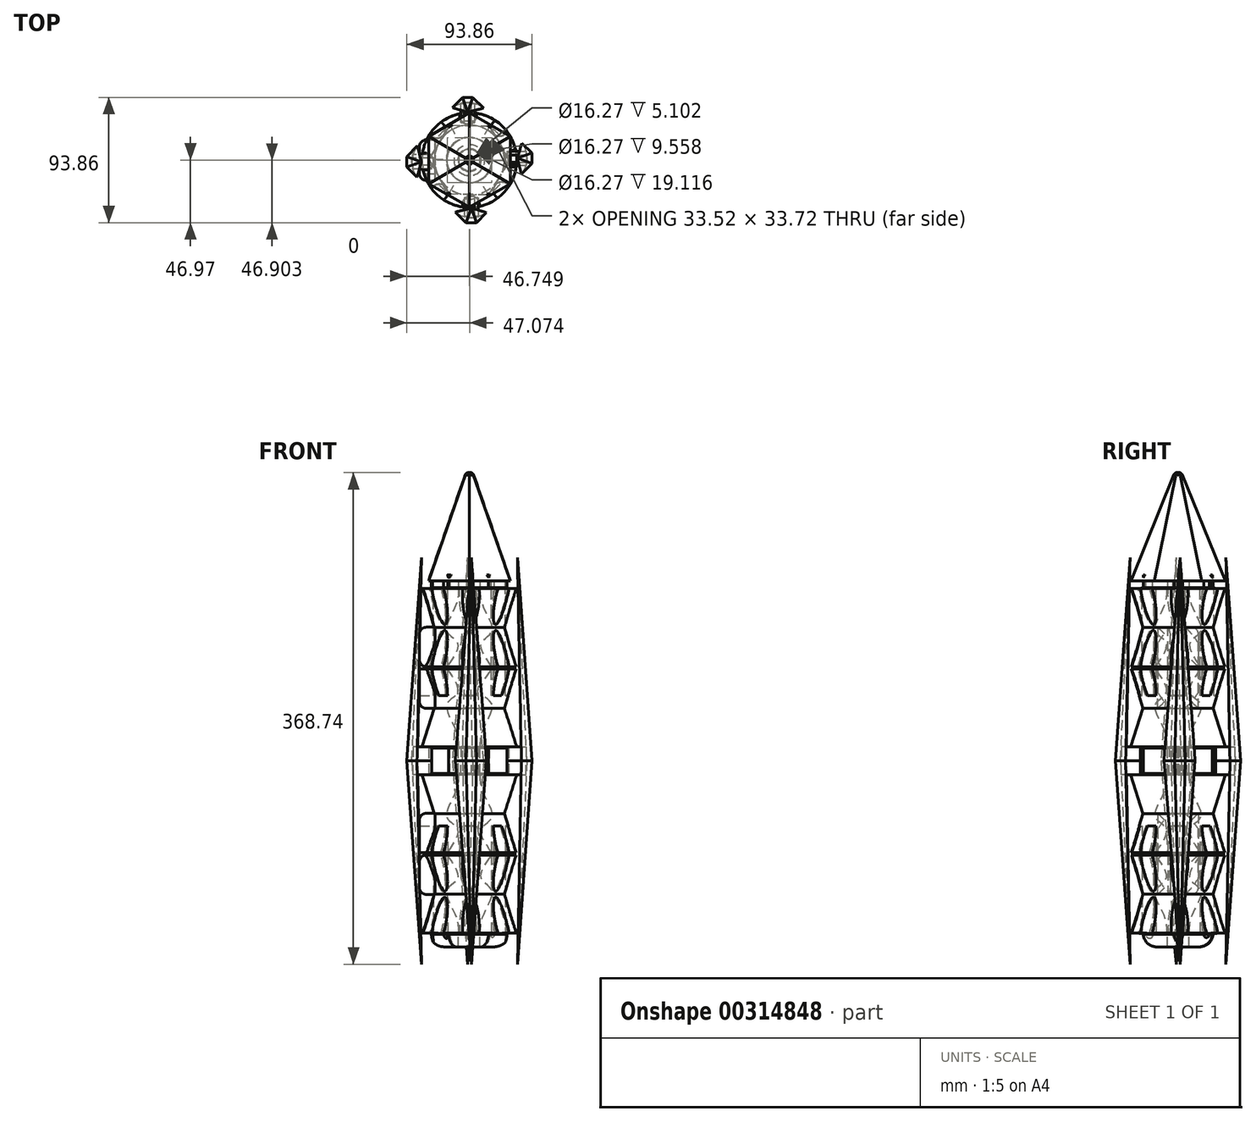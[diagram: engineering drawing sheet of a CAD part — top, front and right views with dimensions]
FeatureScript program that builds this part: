
annotation { "Feature Type Name" : "Feature", "Feature Type Description" : "" }
export const myFeature = defineFeature(function(context is Context, id is Id, definition is map)
    precondition{}
    {
        {
            var Q0;
            Q0=qCreatedBy(makeId("Front.planeOp"),FACE);
            var sketch = newSketch(context, id + "F0", { "sketchPlane" : qUnion([Q0])});
            skLineSegment(sketch, "E0", {"start": v(-35.52, -26.7) * mm, "end": v(-16.9, -26.7) * mm});
            skLineSegment(sketch, "E1", {"start": v(-16.9, 32.53) * mm, "end": v(-35.52, 31.8) * mm});
            skLineSegment(sketch, "E2", {"start": v(-35.52, 31.8) * mm, "end": v(-26.27, 2.74) * mm});
            skLineSegment(sketch, "E3", {"start": v(-26.27, 2.74) * mm, "end": v(-35.52, -26.7) * mm});
            skLineSegment(sketch, "E4", {"start": v(-8.14, 32.78) * mm, "end": v(-16.9, 32.53) * mm});
            skLineSegment(sketch, "E5", {"start": v(0, 39) * mm, "end": v(0, -30.84) * mm});
            skPoint(sketch, "E6.2.internal.orphan", {"position": v(-7.55, 0) * mm});
            skFitSpline(sketch, "E7", {"points": [v(-16.9, -26.7) * mm, v(-8.95, -8.9) * mm, v(-16.9, 0) * mm, v(-10.54, 18.32) * mm, v(-8.14, 32.78) * mm], "startDerivative": vector(53.05, 73.72) * mm, "endDerivative": vector(1.19, 56.97) * mm});
            skSolve(sketch);
        }
        {
            var Q0;
            Q0=makeQuery(id+"F0.imprint","IMPRINT",FACE,{"disambiguationData":[TD([[makeQuery(id+"F0.imprint","IMPRINT",EDGE,{"derivedFrom":sQuery(id+"F0.wireOp",EDGE,"E0")}),1.0]])]});
            var Q1;
            Q1=sQuery(id+"F0.wireOp",EDGE,"E5");
            revolve(context, id + "F1", {"entities" : qUnion([Q0]), "axis" : qUnion([Q1]), "revolveType" : RevolveType.FULL});
        }
        {
            var Q0;
            Q0=qCreatedBy(makeId("Top.planeOp"),FACE);
            cPlane(context, id + "F2", {"entities" : qUnion([Q0]), "cplaneType" : CPlaneType.OFFSET, "offset" : 32.68 * mm, "width" : 152.4 * mm, "height" : 152.4 * mm});
        }
        {
            var Q0;
            Q0=qCreatedBy(id+"F2.planeOp",FACE);
            var sketch = newSketch(context, id + "F3", { "sketchPlane" : qUnion([Q0])});
            skCircle(sketch, "E8.cCircle", {"center": v(-0.18, 0.04) * mm, "radius": 29.91 * mm, "construction": true});
            skLineSegment(sketch, "E8.0", {"start": v(15.3, 25.63) * mm, "end": v(29.72, -0.57) * mm});
            skLineSegment(sketch, "E8.1", {"start": v(29.72, -0.57) * mm, "end": v(14.24, -26.16) * mm});
            skLineSegment(sketch, "E8.2", {"start": v(14.24, -26.16) * mm, "end": v(-15.66, -25.55) * mm});
            skLineSegment(sketch, "E8.3", {"start": v(-15.66, -25.55) * mm, "end": v(-30.09, 0.65) * mm});
            skLineSegment(sketch, "E8.4", {"start": v(-30.09, 0.65) * mm, "end": v(-14.6, 26.25) * mm});
            skLineSegment(sketch, "E8.5", {"start": v(-14.6, 26.25) * mm, "end": v(15.3, 25.63) * mm});
            skCircle(sketch, "E9", {"center": v(-0.18, 0.04) * mm, "radius": 8.14 * mm});
            skSolve(sketch);
        }
        {
            var Q0;
            Q0=makeQuery(id+"F3.imprint","IMPRINT",FACE,{"disambiguationData":[TD([[makeQuery(id+"F3.imprint","IMPRINT",EDGE,{"derivedFrom":sQuery(id+"F3.wireOp",EDGE,"E8.0")}),-1.0]])]});
            extrude(context, id + "F4", {"entities" : qUnion([Q0]), "operationType" : NewBodyOperationType.ADD, "depth" : 9.56 * mm});
        }
        {
            var Q0;
            Q0=qCreatedBy(makeId("Front.planeOp"),FACE);
            var sketch = newSketch(context, id + "F5", { "sketchPlane" : qUnion([Q0])});
            skLineSegment(sketch, "E10.bottom", {"start": v(-25.84, 2.9) * mm, "end": v(-37.47, 2.9) * mm});
            skLineSegment(sketch, "E10.top", {"start": v(-25.84, -26.7) * mm, "end": v(-37.47, -26.7) * mm});
            skLineSegment(sketch, "E10.left", {"start": v(-25.84, 2.9) * mm, "end": v(-25.84, -26.7) * mm});
            skLineSegment(sketch, "E10.right", {"start": v(-37.47, 2.9) * mm, "end": v(-37.47, -26.7) * mm});
            skSolve(sketch);
        }
        {
            var Q0;
            Q0=makeQuery(id+"F5.imprint","IMPRINT",FACE,{"disambiguationData":[TD([[makeQuery(id+"F5.imprint","IMPRINT",EDGE,{"derivedFrom":sQuery(id+"F5.wireOp",EDGE,"E10.bottom")}),1.0]])]});
            extrude(context, id + "F6", {"entities" : qUnion([Q0]), "operationType" : NewBodyOperationType.ADD, "endBound" : BoundingType.SYMMETRIC, "depth" : 30.43 * mm});
        }
        {
            var Q0;
            Q0=makeQuery(id+"F1.opRevolve","SWEPT_FACE",FACE,{"disambiguationData":[OSD([sQuery(id+"F0.wireOp",EDGE,"E0")])]});
            cPlane(context, id + "F7", {"entities" : qUnion([Q0]), "cplaneType" : CPlaneType.OFFSET, "offset" : 0.85 * mm, "width" : 152.4 * mm, "height" : 152.4 * mm});
        }
        {
            var Q0;
            Q0=makeQuery(id+"F1.opRevolve","SWEPT_BODY",BODY,{"disambiguationData":[OSD([sQuery(id+"F0.wireOp",EDGE,"E0"),sQuery(id+"F0.wireOp",EDGE,"E1"),sQuery(id+"F0.wireOp",EDGE,"E2"),sQuery(id+"F0.wireOp",EDGE,"E3"),sQuery(id+"F0.wireOp",EDGE,"E4"),sQuery(id+"F0.wireOp",EDGE,"E7")])]});
            var Q1;
            Q1=qCreatedBy(id+"F7.planeOp",FACE);
            mirror(context, id + "F8", {"entities" : qUnion([Q0]), "mirrorPlane" : qUnion([Q1])});
        }
        {
            var Q0;
            Q0=qCreatedBy(makeId("Top.planeOp"),FACE);
            var sketch = newSketch(context, id + "F9", { "sketchPlane" : qUnion([Q0])});
            skCircle(sketch, "E11", {"center": v(-33.27, -1.11) * mm, "radius": 6.35 * mm});
            skSolve(sketch);
        }
        {
            var Q0;
            Q0 = qSketchRegion(id + "F9", true);
            extrude(context, id + "F10", {"entities" : qUnion([Q0]), "endBound" : BoundingType.SYMMETRIC, "oppositeDirection" : true, "depth" : 97.03 * mm});
        }
        {
            var Q0;
            Q0=makeQuery(id+"F10.opExtrude","CAP_EDGE",EDGE,{"disambiguationData":[OSD([sQuery(id+"F9.wireOp",EDGE,"E11")])],"isStart":true});
            fillet(context, id + "F11", {"entities" : qUnion([Q0]), "radius" : 5.08 * mm, "tangentPropagation" : true, "allowEdgeOverflow" : false});
        }
        {
            var Q0;
            Q0=makeQuery(id+"F6.opExtrude","SWEPT_EDGE",EDGE,{"disambiguationData":[OSD([sQuery(id+"F5.wireOp",EDGE,"E10.bottom"),sQuery(id+"F5.wireOp",EDGE,"E10.right")])]});
            var Q1;
            Q1=makeQuery(id+"F8.opPattern","COPY",EDGE,{"derivedFrom":makeQuery(id+"F6.opExtrude","SWEPT_EDGE",EDGE,{"disambiguationData":[OSD([sQuery(id+"F5.wireOp",EDGE,"E10.bottom"),sQuery(id+"F5.wireOp",EDGE,"E10.right")])]}),"instanceName":"1"});
            var Q2;
            Q2=makeQuery(id+"F8.opPattern","COPY",EDGE,{"derivedFrom":makeQuery(id+"F6.opExtrude","CAP_EDGE",EDGE,{"disambiguationData":[OSD([sQuery(id+"F5.wireOp",EDGE,"E10.right")])],"isStart":false}),"instanceName":"1"});
            var Q3;
            Q3=makeQuery(id+"F6.opExtrude","CAP_EDGE",EDGE,{"disambiguationData":[OSD([sQuery(id+"F5.wireOp",EDGE,"E10.right")])],"isStart":false});
            var Q4;
            Q4=makeQuery(id+"F8.opPattern","COPY",EDGE,{"derivedFrom":makeQuery(id+"F6.opExtrude","CAP_EDGE",EDGE,{"disambiguationData":[OSD([sQuery(id+"F5.wireOp",EDGE,"E10.right")])],"isStart":true}),"instanceName":"1"});
            fillet(context, id + "F12", {"entities" : qUnion([Q0, Q1, Q2, Q3, Q4]), "radius" : 5.08 * mm, "tangentPropagation" : true, "allowEdgeOverflow" : false});
        }
        {
            var Q0;
            Q0=makeQuery(id+"F6.opExtrude","SWEPT_FACE",FACE,{"disambiguationData":[OSD([sQuery(id+"F5.wireOp",EDGE,"E10.right")])]});
            fillet(context, id + "F13", {"entities" : qUnion([Q0]), "radius" : 5.08 * mm, "tangentPropagation" : true, "allowEdgeOverflow" : false});
        }
        {
            var Q0;
            Q0=makeQuery(id+"F10.opExtrude","SWEPT_BODY",BODY,{"disambiguationData":[OSD([sQuery(id+"F9.wireOp",EDGE,"E11")])]});
            var Q1;
            Q1=makeQuery(id+"F8.opPattern","COPY",EDGE,{"derivedFrom":makeQuery(id+"F1.opRevolve","SWEPT_EDGE",EDGE,{"disambiguationData":[OSD([sQuery(id+"F0.wireOp",EDGE,"E0"),sQuery(id+"F0.wireOp",EDGE,"E3")])]}),"instanceName":"1"});
            circularPattern(context, id + "F14", {"entities" : qUnion([Q0]), "axis" : qUnion([Q1]), "angle" : 360 * degree, "instanceCount" : 8, "equalSpace" : true});
        }
        {
            var Q0;
            Q0=makeQuery(id+"F14.opPattern","COPY",BODY,{"derivedFrom":makeQuery(id+"F10.opExtrude","SWEPT_BODY",BODY,{"disambiguationData":[OSD([sQuery(id+"F9.wireOp",EDGE,"E11")])]}),"instanceName":"7"});
            var Q1;
            Q1=makeQuery(id+"F14.opPattern","COPY",BODY,{"derivedFrom":makeQuery(id+"F10.opExtrude","SWEPT_BODY",BODY,{"disambiguationData":[OSD([sQuery(id+"F9.wireOp",EDGE,"E11")])]}),"instanceName":"6"});
            var Q2;
            Q2=makeQuery(id+"F14.opPattern","COPY",BODY,{"derivedFrom":makeQuery(id+"F10.opExtrude","SWEPT_BODY",BODY,{"disambiguationData":[OSD([sQuery(id+"F9.wireOp",EDGE,"E11")])]}),"instanceName":"5"});
            var Q3;
            Q3=makeQuery(id+"F14.opPattern","COPY",BODY,{"derivedFrom":makeQuery(id+"F10.opExtrude","SWEPT_BODY",BODY,{"disambiguationData":[OSD([sQuery(id+"F9.wireOp",EDGE,"E11")])]}),"instanceName":"4"});
            var Q4;
            Q4=makeQuery(id+"F14.opPattern","COPY",BODY,{"derivedFrom":makeQuery(id+"F10.opExtrude","SWEPT_BODY",BODY,{"disambiguationData":[OSD([sQuery(id+"F9.wireOp",EDGE,"E11")])]}),"instanceName":"3"});
            var Q5;
            Q5=makeQuery(id+"F14.opPattern","COPY",BODY,{"derivedFrom":makeQuery(id+"F10.opExtrude","SWEPT_BODY",BODY,{"disambiguationData":[OSD([sQuery(id+"F9.wireOp",EDGE,"E11")])]}),"instanceName":"2"});
            var Q6;
            Q6=makeQuery(id+"F14.opPattern","COPY",BODY,{"derivedFrom":makeQuery(id+"F10.opExtrude","SWEPT_BODY",BODY,{"disambiguationData":[OSD([sQuery(id+"F9.wireOp",EDGE,"E11")])]}),"instanceName":"1"});
            var Q7;
            Q7=makeQuery(id+"F10.opExtrude","SWEPT_BODY",BODY,{"disambiguationData":[OSD([sQuery(id+"F9.wireOp",EDGE,"E11")])]});
            var Q8;
            Q8=makeQuery(id+"F8.opPattern","COPY",BODY,{"derivedFrom":makeQuery(id+"F1.opRevolve","SWEPT_BODY",BODY,{"disambiguationData":[OSD([sQuery(id+"F0.wireOp",EDGE,"E0"),sQuery(id+"F0.wireOp",EDGE,"E1"),sQuery(id+"F0.wireOp",EDGE,"E2"),sQuery(id+"F0.wireOp",EDGE,"E3"),sQuery(id+"F0.wireOp",EDGE,"E4"),sQuery(id+"F0.wireOp",EDGE,"E7")])]}),"instanceName":"1"});
            var Q9;
            Q9=makeQuery(id+"F1.opRevolve","SWEPT_BODY",BODY,{"disambiguationData":[OSD([sQuery(id+"F0.wireOp",EDGE,"E0"),sQuery(id+"F0.wireOp",EDGE,"E1"),sQuery(id+"F0.wireOp",EDGE,"E2"),sQuery(id+"F0.wireOp",EDGE,"E3"),sQuery(id+"F0.wireOp",EDGE,"E4"),sQuery(id+"F0.wireOp",EDGE,"E7")])]});
            booleanBodies(context, id + "F15", {"operationType" : BooleanOperationType.SUBTRACTION, "tools" : qUnion([Q0, Q1, Q2, Q3, Q4, Q5, Q6, Q7]), "targets" : qUnion([Q8, Q9])});
        }
        {
            var Q0;
            Q0=makeQuery(id+"F8.opPattern","COPY",FACE,{"derivedFrom":makeQuery(id+"F4.opExtrude","CAP_FACE",FACE,{"disambiguationData":[OSD([sQuery(id+"F3.wireOp",EDGE,"E8.0"),sQuery(id+"F3.wireOp",EDGE,"E8.1"),sQuery(id+"F3.wireOp",EDGE,"E8.2"),sQuery(id+"F3.wireOp",EDGE,"E8.3"),sQuery(id+"F3.wireOp",EDGE,"E8.4"),sQuery(id+"F3.wireOp",EDGE,"E8.5"),sQuery(id+"F3.wireOp",EDGE,"E9")])],"isStart":false}),"instanceName":"1"});
            cPlane(context, id + "F16", {"entities" : qUnion([Q0]), "cplaneType" : CPlaneType.OFFSET, "offset" : 0 * mm, "width" : 150 * mm, "height" : 150 * mm});
        }
        {
            var Q0;
            Q0=makeQuery(id+"F1.opRevolve","SWEPT_BODY",BODY,{"disambiguationData":[OSD([sQuery(id+"F0.wireOp",EDGE,"E0"),sQuery(id+"F0.wireOp",EDGE,"E1"),sQuery(id+"F0.wireOp",EDGE,"E2"),sQuery(id+"F0.wireOp",EDGE,"E3"),sQuery(id+"F0.wireOp",EDGE,"E4"),sQuery(id+"F0.wireOp",EDGE,"E7")])]});
            var Q1;
            Q1=makeQuery(id+"F8.opPattern","COPY",BODY,{"derivedFrom":makeQuery(id+"F1.opRevolve","SWEPT_BODY",BODY,{"disambiguationData":[OSD([sQuery(id+"F0.wireOp",EDGE,"E0"),sQuery(id+"F0.wireOp",EDGE,"E1"),sQuery(id+"F0.wireOp",EDGE,"E2"),sQuery(id+"F0.wireOp",EDGE,"E3"),sQuery(id+"F0.wireOp",EDGE,"E4"),sQuery(id+"F0.wireOp",EDGE,"E7")])]}),"instanceName":"1"});
            var Q2;
            Q2=qCreatedBy(id+"F16.planeOp",FACE);
            mirror(context, id + "F17", {"operationType" : NewBodyOperationType.ADD, "entities" : qUnion([Q0, Q1]), "mirrorPlane" : qUnion([Q2])});
        }
        {
            var Q0;
            Q0=qCreatedBy(id+"F16.planeOp",FACE);
            var sketch = newSketch(context, id + "F18", { "sketchPlane" : qUnion([Q0])});
            skLineSegment(sketch, "E12.bottom", {"start": v(-6.56, -28.3) * mm, "end": v(-3.83, -28.3) * mm});
            skLineSegment(sketch, "E12.top", {"start": v(-6.56, -42.42) * mm, "end": v(-3.83, -42.42) * mm});
            skLineSegment(sketch, "E12.left", {"start": v(-6.56, -28.3) * mm, "end": v(-6.56, -42.42) * mm});
            skLineSegment(sketch, "E12.right", {"start": v(-3.83, -28.3) * mm, "end": v(-3.83, -42.42) * mm});
            skLineSegment(sketch, "E13.bottom", {"start": v(1.55, -28.3) * mm, "end": v(3.99, -28.3) * mm});
            skLineSegment(sketch, "E13.top", {"start": v(1.55, -42.4) * mm, "end": v(3.99, -42.4) * mm});
            skLineSegment(sketch, "E13.left", {"start": v(1.55, -28.3) * mm, "end": v(1.55, -42.4) * mm});
            skLineSegment(sketch, "E13.right", {"start": v(3.99, -28.3) * mm, "end": v(3.99, -42.4) * mm});
            skArc(sketch, "E14", {"start": v(-12.8, -39.34) * mm, "mid": v(-1.04, -43.17) * mm, "end": v(10.6, -39) * mm});
            skLineSegment(sketch, "E15", {"start": v(-12.8, -39.34) * mm, "end": v(-5.25, -46.93) * mm});
            skLineSegment(sketch, "E16", {"start": v(-5.25, -46.93) * mm, "end": v(2.51, -46.93) * mm});
            skLineSegment(sketch, "E17", {"start": v(2.51, -46.93) * mm, "end": v(10.6, -39) * mm});
            skPoint(sketch, "E18", {"position": v(-1.37, -45.2) * mm});
            skPoint(sketch, "E18.positionSnap0", {"position": v(-1.37, -46.93) * mm});
            skSolve(sketch);
        }
        {
            var Q0;
            Q0=qCreatedBy(id+"F16.planeOp",FACE);
            cPlane(context, id + "F19", {"entities" : qUnion([Q0]), "cplaneType" : CPlaneType.OFFSET, "offset" : 152.56 * mm, "width" : 150 * mm, "height" : 150 * mm});
        }
        {
            var Q0;
            Q0=qCreatedBy(id+"F19.planeOp",FACE);
            var sketch = newSketch(context, id + "F20", { "sketchPlane" : qUnion([Q0])});
            skPoint(sketch, "E19", {"position": v(-1.42, -35.99) * mm});
            skSolve(sketch);
        }
        {
            var Q0;
            Q0=makeQuery(id+"F18.imprint","IMPRINT",FACE,{"disambiguationData":[TD([[makeQuery(id+"F18.imprint","IMPRINT",EDGE,{"derivedFrom":sQuery(id+"F18.wireOp",EDGE,"E14")}),-1.0]])]});
            var Q1;
            Q1=sQuery(id+"F20.wireOp",VERTEX,"E19");
            loft(context, id + "F21", {"sheetProfilesArray" : [{ "sheetProfileEntities" : qUnion([Q0]) }, { "sheetProfileEntities" : qUnion([Q1]) }]});
        }
        {
            var Q0;
            Q0=makeQuery(id+"F18.imprint","IMPRINT",FACE,{"disambiguationData":[TD([[makeQuery(id+"F18.imprint","IMPRINT",EDGE,{"derivedFrom":sQuery(id+"F18.wireOp",EDGE,"E12.bottom")}),-1.0]])]});
            var Q1;
            Q1=makeQuery(id+"F18.imprint","IMPRINT",FACE,{"disambiguationData":[TD([[makeQuery(id+"F18.imprint","IMPRINT",EDGE,{"derivedFrom":sQuery(id+"F18.wireOp",EDGE,"E13.bottom")}),-1.0]])]});
            extrude(context, id + "F22", {"entities" : qUnion([Q0, Q1]), "depth" : 10.53 * mm});
        }
        {
            var Q0;
            Q0=makeQuery(id+"F21.opLoft","SWEPT_BODY",BODY,{"disambiguationData":[OSD([makeQuery(id+"F18.imprint","IMPRINT",FACE,{"disambiguationData":[TD([[makeQuery(id+"F18.imprint","IMPRINT",EDGE,{"derivedFrom":sQuery(id+"F18.wireOp",EDGE,"E14")}),-1.0]])]}),sQuery(id+"F20.wireOp",VERTEX,"E19")])]});
            var Q1;
            Q1=makeQuery(id+"F22.opExtrude","SWEPT_BODY",BODY,{"disambiguationData":[OSD([sQuery(id+"F18.wireOp",EDGE,"E12.bottom"),sQuery(id+"F18.wireOp",EDGE,"E12.top"),sQuery(id+"F18.wireOp",EDGE,"E12.left"),sQuery(id+"F18.wireOp",EDGE,"E12.right")])]});
            var Q2;
            Q2=makeQuery(id+"F22.opExtrude","SWEPT_BODY",BODY,{"disambiguationData":[OSD([sQuery(id+"F18.wireOp",EDGE,"E13.bottom"),sQuery(id+"F18.wireOp",EDGE,"E13.top"),sQuery(id+"F18.wireOp",EDGE,"E13.left"),sQuery(id+"F18.wireOp",EDGE,"E13.right")])]});
            var Q3;
            Q3=qCreatedBy(id+"F16.planeOp",FACE);
            mirror(context, id + "F23", {"entities" : qUnion([Q0, Q1, Q2]), "mirrorPlane" : qUnion([Q3])});
        }
        {
            var Q0;
            Q0=makeQuery(id+"F21.opLoft","SWEPT_BODY",BODY,{"disambiguationData":[OSD([makeQuery(id+"F18.imprint","IMPRINT",FACE,{"disambiguationData":[TD([[makeQuery(id+"F18.imprint","IMPRINT",EDGE,{"derivedFrom":sQuery(id+"F18.wireOp",EDGE,"E14")}),-1.0]])]}),sQuery(id+"F20.wireOp",VERTEX,"E19")])]});
            var Q1;
            Q1=makeQuery(id+"F23.opPattern","COPY",BODY,{"derivedFrom":makeQuery(id+"F21.opLoft","SWEPT_BODY",BODY,{"disambiguationData":[OSD([makeQuery(id+"F18.imprint","IMPRINT",FACE,{"disambiguationData":[TD([[makeQuery(id+"F18.imprint","IMPRINT",EDGE,{"derivedFrom":sQuery(id+"F18.wireOp",EDGE,"E14")}),-1.0]])]}),sQuery(id+"F20.wireOp",VERTEX,"E19")])]}),"instanceName":"1"});
            var Q2;
            Q2=makeQuery(id+"F22.opExtrude","SWEPT_BODY",BODY,{"disambiguationData":[OSD([sQuery(id+"F18.wireOp",EDGE,"E12.bottom"),sQuery(id+"F18.wireOp",EDGE,"E12.top"),sQuery(id+"F18.wireOp",EDGE,"E12.left"),sQuery(id+"F18.wireOp",EDGE,"E12.right")])]});
            var Q3;
            Q3=makeQuery(id+"F23.opPattern","COPY",BODY,{"derivedFrom":makeQuery(id+"F22.opExtrude","SWEPT_BODY",BODY,{"disambiguationData":[OSD([sQuery(id+"F18.wireOp",EDGE,"E12.bottom"),sQuery(id+"F18.wireOp",EDGE,"E12.top"),sQuery(id+"F18.wireOp",EDGE,"E12.left"),sQuery(id+"F18.wireOp",EDGE,"E12.right")])]}),"instanceName":"1"});
            var Q4;
            Q4=makeQuery(id+"F23.opPattern","COPY",BODY,{"derivedFrom":makeQuery(id+"F22.opExtrude","SWEPT_BODY",BODY,{"disambiguationData":[OSD([sQuery(id+"F18.wireOp",EDGE,"E13.bottom"),sQuery(id+"F18.wireOp",EDGE,"E13.top"),sQuery(id+"F18.wireOp",EDGE,"E13.left"),sQuery(id+"F18.wireOp",EDGE,"E13.right")])]}),"instanceName":"1"});
            var Q5;
            Q5=makeQuery(id+"F22.opExtrude","SWEPT_BODY",BODY,{"disambiguationData":[OSD([sQuery(id+"F18.wireOp",EDGE,"E13.bottom"),sQuery(id+"F18.wireOp",EDGE,"E13.top"),sQuery(id+"F18.wireOp",EDGE,"E13.left"),sQuery(id+"F18.wireOp",EDGE,"E13.right")])]});
            var Q6;
            Q6=makeQuery(id+"F17.opPattern","COPY",EDGE,{"derivedFrom":makeQuery(id+"F8.opPattern","COPY",EDGE,{"derivedFrom":makeQuery(id+"F1.opRevolve","SWEPT_EDGE",EDGE,{"disambiguationData":[OSD([sQuery(id+"F0.wireOp",EDGE,"E1"),sQuery(id+"F0.wireOp",EDGE,"E2")])]}),"instanceName":"1"}),"instanceName":"1"});
            circularPattern(context, id + "F24", {"entities" : qUnion([Q0, Q1, Q2, Q3, Q4, Q5]), "axis" : qUnion([Q6]), "angle" : 360 * degree, "instanceCount" : 4, "equalSpace" : true});
        }
        {
            var Q0;
            Q0=qCreatedBy(makeId("Top.planeOp"),FACE);
            cPlane(context, id + "F25", {"entities" : qUnion([Q0]), "cplaneType" : CPlaneType.OFFSET, "offset" : 37.78 * mm, "width" : 150 * mm, "height" : 150 * mm});
        }
        {
            var Q0;
            Q0=qCreatedBy(id+"F25.planeOp",FACE);
            var sketch = newSketch(context, id + "F26", { "sketchPlane" : qUnion([Q0])});
            skCircle(sketch, "E20.cCircle", {"center": v(0, 0) * mm, "radius": 30.65 * mm, "construction": true});
            skLineSegment(sketch, "E20.0", {"start": v(-30.65, -17.7) * mm, "end": v(-30.65, 17.7) * mm});
            skLineSegment(sketch, "E20.1", {"start": v(-30.65, 17.7) * mm, "end": v(0, 35.39) * mm});
            skLineSegment(sketch, "E20.2", {"start": v(0, 35.39) * mm, "end": v(30.65, 17.7) * mm});
            skLineSegment(sketch, "E20.3", {"start": v(30.65, 17.7) * mm, "end": v(30.65, -17.7) * mm});
            skLineSegment(sketch, "E20.4", {"start": v(30.65, -17.7) * mm, "end": v(0, -35.39) * mm});
            skLineSegment(sketch, "E20.5", {"start": v(0, -35.39) * mm, "end": v(-30.65, -17.7) * mm});
            skPoint(sketch, "E20.0.midPoint", {"position": v(-30.65, 0) * mm});
            skSolve(sketch);
        }
        {
            var Q0;
            Q0=qCreatedBy(id+"F25.planeOp",FACE);
            cPlane(context, id + "F27", {"entities" : qUnion([Q0]), "cplaneType" : CPlaneType.OFFSET, "offset" : 81.08 * mm, "width" : 150 * mm, "height" : 150 * mm});
        }
        {
            var Q0;
            Q0=qCreatedBy(id+"F27.planeOp",FACE);
            var sketch = newSketch(context, id + "F28", { "sketchPlane" : qUnion([Q0])});
            skCircle(sketch, "E21", {"center": v(0, 0) * mm, "radius": 2.56 * mm});
            skSolve(sketch);
        }
        {
            var Q1;
            Q1 = qSketchRegion(id + "F26", true);
            var Q2;
            Q2 = qSketchRegion(id + "F28", true);
            loft(context, id + "F29", {"operationType" : NewBodyOperationType.ADD, "sheetProfilesArray" : [{ "sheetProfileEntities" : qUnion([Q1]) }, { "sheetProfileEntities" : qUnion([Q2]) }]});
        }
        {
            var Q0;
            Q0=makeQuery(id+"F29.opLoft","MID_CAP_EDGE",EDGE,{"disambiguationData":[OSD([sQuery(id+"F26.wireOp",EDGE,"E20.3"),sQuery(id+"F26.wireOp",EDGE,"E20.4"),sQuery(id+"F26.wireOp",EDGE,"E20.5"),sQuery(id+"F28.wireOp",EDGE,"E21")])],"capPos":1.0});
            var Q1;
            Q1=makeQuery(id+"F29.opLoft","MID_CAP_EDGE",EDGE,{"disambiguationData":[OSD([sQuery(id+"F26.wireOp",EDGE,"E20.2"),sQuery(id+"F26.wireOp",EDGE,"E20.3"),sQuery(id+"F26.wireOp",EDGE,"E20.4"),sQuery(id+"F28.wireOp",EDGE,"E21")])],"capPos":1.0});
            var Q2;
            Q2=makeQuery(id+"F29.opLoft","MID_CAP_EDGE",EDGE,{"disambiguationData":[OSD([sQuery(id+"F26.wireOp",EDGE,"E20.1"),sQuery(id+"F26.wireOp",EDGE,"E20.2"),sQuery(id+"F26.wireOp",EDGE,"E20.3"),sQuery(id+"F28.wireOp",EDGE,"E21")])],"capPos":1.0});
            var Q3;
            Q3=makeQuery(id+"F29.opLoft","CAP_FACE",FACE,{"disambiguationData":[OSD([makeQuery(id+"F28.imprint","IMPRINT",FACE,{"disambiguationData":[TD([[makeQuery(id+"F28.imprint","IMPRINT",EDGE,{"derivedFrom":sQuery(id+"F28.wireOp",EDGE,"E21")}),1.0]])]})])],"isStart":true});
            var Q4;
            Q4=makeQuery(id+"F29.opLoft","MID_CAP_EDGE",EDGE,{"disambiguationData":[OSD([sQuery(id+"F26.wireOp",EDGE,"E20.0"),sQuery(id+"F26.wireOp",EDGE,"E20.5"),sQuery(id+"F28.wireOp",EDGE,"E21")])],"capPos":1.0});
            var Q5;
            Q5=makeQuery(id+"F29.opLoft","MID_CAP_EDGE",EDGE,{"disambiguationData":[OSD([sQuery(id+"F26.wireOp",EDGE,"E20.0"),sQuery(id+"F26.wireOp",EDGE,"E20.4"),sQuery(id+"F26.wireOp",EDGE,"E20.5"),sQuery(id+"F28.wireOp",EDGE,"E21")])],"capPos":1.0});
            var Q6;
            Q6=makeQuery(id+"F29.opLoft","MID_CAP_EDGE",EDGE,{"disambiguationData":[OSD([sQuery(id+"F26.wireOp",EDGE,"E20.0"),sQuery(id+"F26.wireOp",EDGE,"E20.1"),sQuery(id+"F26.wireOp",EDGE,"E20.2"),sQuery(id+"F26.wireOp",EDGE,"E20.5"),sQuery(id+"F28.wireOp",EDGE,"E21")])],"capPos":1.0});
            fillet(context, id + "F30", {"entities" : qUnion([Q0, Q1, Q2, Q3, Q4, Q5, Q6]), "radius" : 2.5 * mm, "tangentPropagation" : true, "rho" : 0.5, "crossSection" : FilletCrossSection.CONIC, "allowEdgeOverflow" : false});
        }
        {
            var Q0;
            Q0=makeQuery(id+"F17.opPattern","COPY",EDGE,{"derivedFrom":makeQuery(id+"F4.opExtrude","CAP_EDGE",EDGE,{"disambiguationData":[OSD([sQuery(id+"F3.wireOp",EDGE,"E8.1")])],"isStart":false}),"instanceName":"1"});
            var Q1;
            Q1=makeQuery(id+"F17.opPattern","COPY",EDGE,{"derivedFrom":makeQuery(id+"F4.opExtrude","CAP_EDGE",EDGE,{"disambiguationData":[OSD([sQuery(id+"F3.wireOp",EDGE,"E8.2")])],"isStart":false}),"instanceName":"1"});
            var Q2;
            {var subQ0=sQuery(id+"F3.wireOp",EDGE,"E8.3");var subQ1=makeQuery(id+"F10.opExtrude","SWEPT_FACE",FACE,{"disambiguationData":[OSD([sQuery(id+"F9.wireOp",EDGE,"E11")])]});Q2=makeQuery(id+"F17.opPattern","COPY",EDGE,{"derivedFrom":makeQuery(id+"F15.opBoolean","SPLIT",EDGE,{"disambiguationData":[TD([subQ1])],"derivedFrom":makeQuery(id+"F4.opExtrude","CAP_EDGE",EDGE,{"disambiguationData":[OSD([subQ0])],"isStart":false})}),"instanceName":"1"});}
            var Q3;
            Q3=makeQuery(id+"F17.opPattern","COPY",EDGE,{"derivedFrom":makeQuery(id+"F4.opExtrude","CAP_EDGE",EDGE,{"disambiguationData":[OSD([sQuery(id+"F3.wireOp",EDGE,"E8.4")])],"isStart":false}),"instanceName":"1"});
            var Q4;
            Q4=makeQuery(id+"F17.opPattern","COPY",EDGE,{"derivedFrom":makeQuery(id+"F4.opExtrude","CAP_EDGE",EDGE,{"disambiguationData":[OSD([sQuery(id+"F3.wireOp",EDGE,"E8.5")])],"isStart":false}),"instanceName":"1"});
            var Q5;
            {var subQ0=sQuery(id+"F3.wireOp",EDGE,"E8.0");var subQ1=makeQuery(id+"F10.opExtrude","SWEPT_FACE",FACE,{"disambiguationData":[OSD([sQuery(id+"F9.wireOp",EDGE,"E11")])]});Q5=makeQuery(id+"F17.opPattern","COPY",EDGE,{"derivedFrom":makeQuery(id+"F15.opBoolean","SPLIT",EDGE,{"disambiguationData":[TD([makeQuery(id+"F14.opPattern","COPY",FACE,{"derivedFrom":subQ1,"instanceName":"4"})])],"derivedFrom":makeQuery(id+"F4.opExtrude","CAP_EDGE",EDGE,{"disambiguationData":[OSD([subQ0])],"isStart":false})}),"instanceName":"1"});}
            fillet(context, id + "F31", {"entities" : qUnion([Q0, Q1, Q2, Q3, Q4, Q5]), "radius" : 10 * mm, "tangentPropagation" : true, "allowEdgeOverflow" : false});
        }
    });
